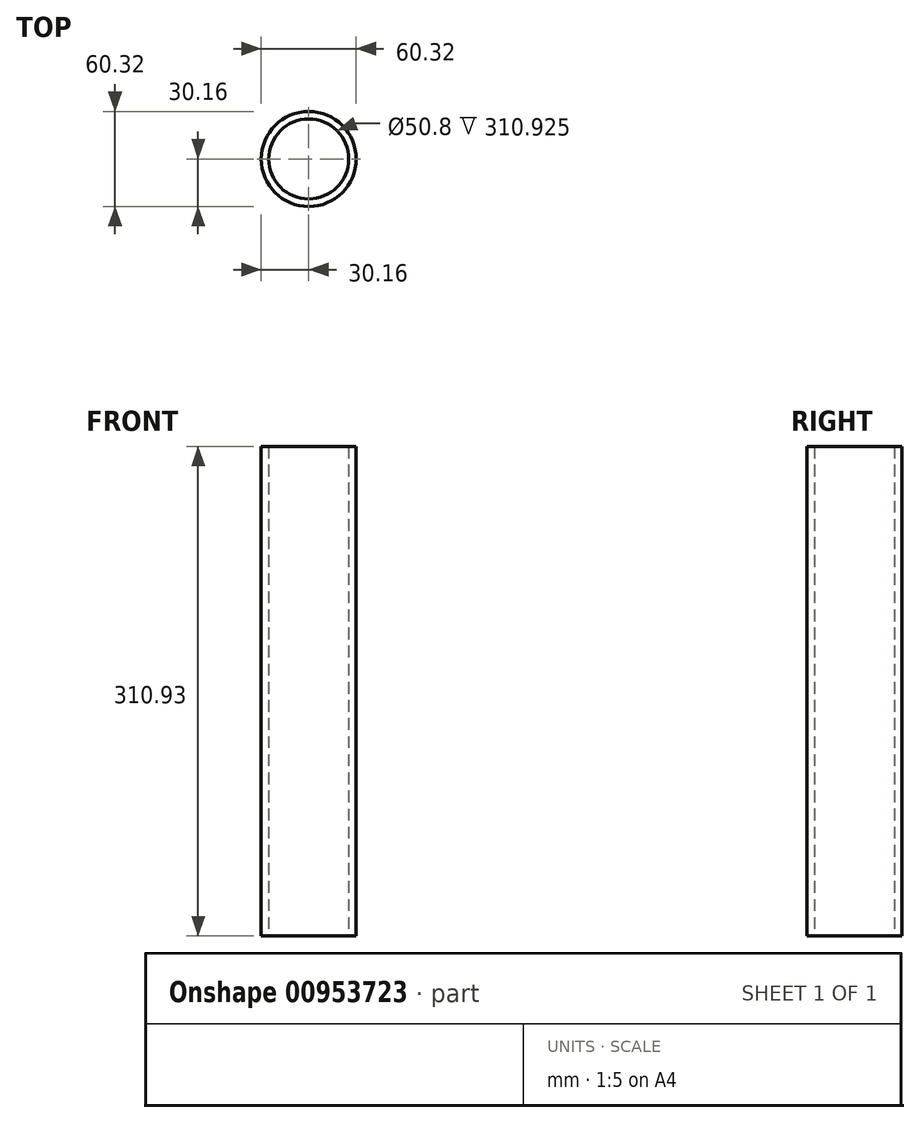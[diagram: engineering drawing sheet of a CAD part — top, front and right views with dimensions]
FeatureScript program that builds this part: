
annotation { "Feature Type Name" : "Feature", "Feature Type Description" : "" }
export const myFeature = defineFeature(function(context is Context, id is Id, definition is map)
    precondition{}
    {
        {
            var Q0;
            Q0=qCreatedBy(makeId("Top.planeOp"),FACE);
            var sketch = newSketch(context, id + "F0", { "sketchPlane" : qUnion([Q0])});
            skCircle(sketch, "E0", {"center": v(0, 0) * mm, "radius": 25.4 * mm});
            skCircle(sketch, "E1", {"center": v(0, 0) * mm, "radius": 30.16 * mm});
            skSolve(sketch);
        }
        {
            var Q0;
            Q0=makeQuery(id+"F0.imprint","IMPRINT",FACE,{"disambiguationData":[TD([[makeQuery(id+"F0.imprint","IMPRINT",EDGE,{"derivedFrom":sQuery(id+"F0.wireOp",EDGE,"E0")}),-1.0]])]});
            extrude(context, id + "F1", {"entities" : qUnion([Q0]), "offsetDistance" : 25 * mm, "depth" : 304.8 * mm, "hasSecondDirection" : true, "secondDirectionOppositeDirection" : true, "secondDirectionDepth" : (6 + (1 / 8)) * mm});
        }
    });
